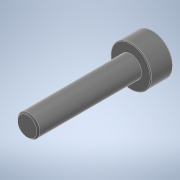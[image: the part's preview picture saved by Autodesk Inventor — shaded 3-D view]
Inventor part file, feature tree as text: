
AUTODESK INVENTOR PART (.ipt)
format: ipt  version: 2022 (Build 260153000, 153)  size: 136,704 bytes
history: native  units: in
note: dims shown in document units (in); Inventor stores cm internally (conversion verified against a paired STEP export)
features: sketch x3, extrude x2, fillet x1, chamfer x1
ambient origin geometry x8: Origin, YZ Plane, XZ Plane, XY Plane, X Axis, Y Axis, Z Axis, Center Point
bodies: Body1 (feature_tree)
feature tree (7):
  extrude  "Extrusion2"  Depth=0.5512in TaperAngle=0.0deg
  extrude  "Extrusion1"  Depth=0.0039in
  fillet  "Fillet1"  Radius=0.0039in
  chamfer  "Chamfer1"  Distance=0.0079in
  sketch  "Sketch1"  dims[d0=0.1181in d1=0.0in d2=0.5512in d3=0.0in]
  sketch  "Sketch2"  dims[d4=0.1181in d5=0.0in d6=0.0039in d7=0.0039in d8=0.0079in d9=0.0079in d10=17.7165in]
  sketch  "Sketch3"
